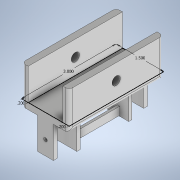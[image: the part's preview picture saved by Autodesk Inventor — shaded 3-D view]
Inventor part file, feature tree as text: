
AUTODESK INVENTOR PART (.ipt)
format: ipt  version: 2020 (Build 240168000, 168)  size: 644,608 bytes
history: native  units: in
note: dims shown in document units (in); Inventor stores cm internally (conversion verified against a paired STEP export)
features: sketch x5, extrude x5, hole x2, fillet x1
ambient origin geometry x8: Origin, YZ Plane, XZ Plane, XY Plane, X Axis, Y Axis, Z Axis, Center Point
bodies: Solid1 (feature_tree)
feature tree (13):
  sketch  "Sketch1"  dims[d0=1.5in d1=3.0in]
  extrude  "Extrusion1"  Depth=3.0in
  extrude  "Extrusion2"  Depth=0.2in
  hole  "Hole1"  [1 undecoded]
  extrude  "Extrusion3"  Depth=0.5in
  hole  "Hole2"  [1 undecoded]
  fillet  "Fillet1"  Radius=0.75in
  extrude  "Extrusion4"  Depth=0.125in
  extrude  "Extrusion5"  Depth=0.125in
  sketch  "Sketch2"  dims[d2=0.2in d3=0.2in]
  sketch  "Sketch3"  dims[d4=1.0in d5=0.0in d6=0.2in d7=0.0in]
  sketch  "Sketch5"  dims[d8=0.5in]
  sketch  "Sketch6"  dims[d9=0.266in d10=0.75in d11=0.438in d12=0.25in d13=0.5635in d14=1.0in d15=0.8108in d16=0.5in d17=1.0in d18=0.75in d19=0.125in d20=0.125in d21=1.0in d22=0.0in d23=0.45in d24=0.1125in d25=0.75in d26=0.438in d27=0.25in d28=0.5635in d29=1.0in d30=0.8108in d31=0.125in d32=0.125in d33=0.125in d34=0.5in d35=0.5in d36=90.0deg d37=0.1in d38=0.1in d39=0.125in d40=0.075in d41=0.25in d42=1.6in d43=0.0in d44=0.05in d45=0.0in d46=0.5in d47=0.5in d48=0.5in d49=0.375in]
note: 2 required parameter values undecoded (feature->parameter linkage not recoverable at this tier; creation-order binding heuristic only, values carry confidence <= 0.55)
